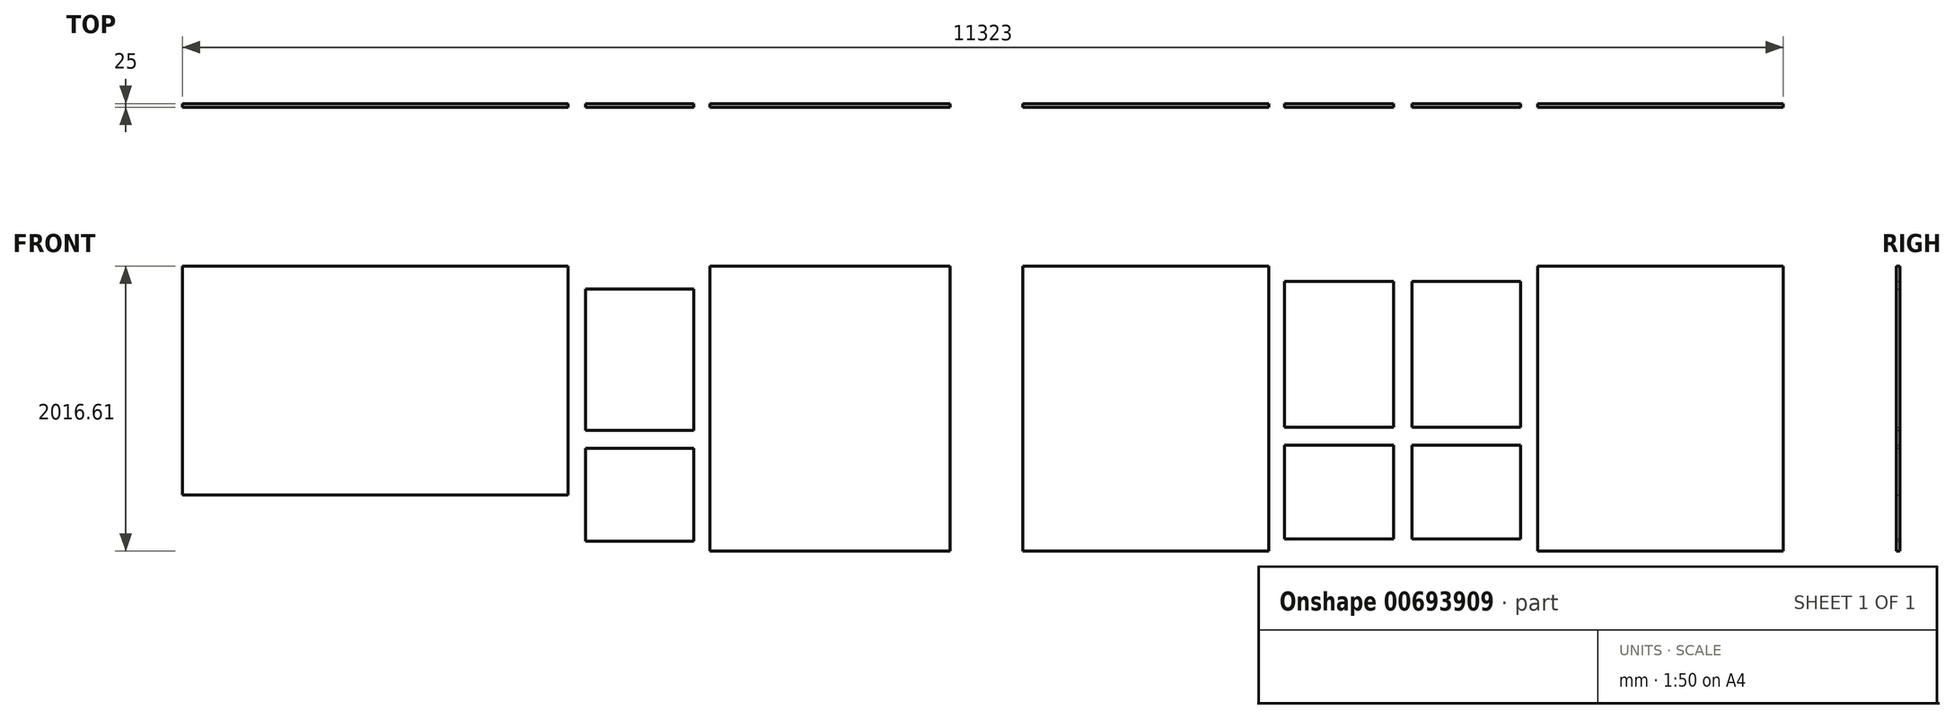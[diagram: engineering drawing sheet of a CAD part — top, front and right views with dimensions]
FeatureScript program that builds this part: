
annotation { "Feature Type Name" : "Feature", "Feature Type Description" : "" }
export const myFeature = defineFeature(function(context is Context, id is Id, definition is map)
    precondition{}
    {
        {
            var Q0;
            Q0=qCreatedBy(makeId("Front.planeOp"),FACE);
            var sketch = newSketch(context, id + "F0", { "sketchPlane" : qUnion([Q0])});
            skLineSegment(sketch, "E0.bottom", {"start": v(514, 2060.6) * mm, "end": v(2253, 2060.6) * mm});
            skLineSegment(sketch, "E0.top", {"start": v(514, 44) * mm, "end": v(2253, 44) * mm});
            skLineSegment(sketch, "E0.left", {"start": v(514, 2060.6) * mm, "end": v(514, 44) * mm});
            skLineSegment(sketch, "E0.right", {"start": v(2253, 2060.6) * mm, "end": v(2253, 44) * mm});
            skLineSegment(sketch, "E1.bottom", {"start": v(2365, 795) * mm, "end": v(3135, 795) * mm});
            skLineSegment(sketch, "E1.top", {"start": v(2365, 130) * mm, "end": v(3135, 130) * mm});
            skLineSegment(sketch, "E1.left", {"start": v(2365, 795) * mm, "end": v(2365, 130) * mm});
            skLineSegment(sketch, "E1.right", {"start": v(3135, 795) * mm, "end": v(3135, 130) * mm});
            skLineSegment(sketch, "E2.bottom", {"start": v(3266, 795) * mm, "end": v(4036, 795) * mm});
            skLineSegment(sketch, "E2.top", {"start": v(3266, 130) * mm, "end": v(4036, 130) * mm});
            skLineSegment(sketch, "E2.left", {"start": v(3266, 795) * mm, "end": v(3266, 130) * mm});
            skLineSegment(sketch, "E2.right", {"start": v(4036, 795) * mm, "end": v(4036, 130) * mm});
            skLineSegment(sketch, "E3.bottom", {"start": v(3266, 1952.8) * mm, "end": v(4036, 1952.8) * mm});
            skLineSegment(sketch, "E3.top", {"start": v(3266, 921) * mm, "end": v(4036, 921) * mm});
            skLineSegment(sketch, "E3.left", {"start": v(3266, 1952.8) * mm, "end": v(3266, 921) * mm});
            skLineSegment(sketch, "E3.right", {"start": v(4036, 1952.8) * mm, "end": v(4036, 921) * mm});
            skLineSegment(sketch, "E4.bottom", {"start": v(2365, 1952.8) * mm, "end": v(3135, 1952.8) * mm});
            skLineSegment(sketch, "E4.top", {"start": v(2365, 921) * mm, "end": v(3135, 921) * mm});
            skLineSegment(sketch, "E4.left", {"start": v(2365, 1952.8) * mm, "end": v(2365, 921) * mm});
            skLineSegment(sketch, "E4.right", {"start": v(3135, 1952.8) * mm, "end": v(3135, 921) * mm});
            skLineSegment(sketch, "E5.bottom", {"start": v(4156, 2060.6) * mm, "end": v(5892, 2060.6) * mm});
            skLineSegment(sketch, "E5.top", {"start": v(4156, 44) * mm, "end": v(5892, 44) * mm});
            skLineSegment(sketch, "E5.left", {"start": v(4156, 2060.6) * mm, "end": v(4156, 44) * mm});
            skLineSegment(sketch, "E5.right", {"start": v(5892, 2060.6) * mm, "end": v(5892, 44) * mm});
            skLineSegment(sketch, "E6.bottom", {"start": v(-1700, 2060.6) * mm, "end": v(0, 2060.6) * mm});
            skLineSegment(sketch, "E6.top", {"start": v(-1700, 44) * mm, "end": v(0, 44) * mm});
            skLineSegment(sketch, "E6.left", {"start": v(-1700, 2060.6) * mm, "end": v(-1700, 44) * mm});
            skLineSegment(sketch, "E6.right", {"start": v(0, 2060.6) * mm, "end": v(0, 44) * mm});
            skLineSegment(sketch, "E7.bottom", {"start": v(-2579, 1898) * mm, "end": v(-1814, 1898) * mm});
            skLineSegment(sketch, "E7.top", {"start": v(-2579, 898) * mm, "end": v(-1814, 898) * mm});
            skLineSegment(sketch, "E7.left", {"start": v(-2579, 1898) * mm, "end": v(-2579, 898) * mm});
            skLineSegment(sketch, "E7.right", {"start": v(-1814, 1898) * mm, "end": v(-1814, 898) * mm});
            skLineSegment(sketch, "E8.bottom", {"start": v(-2579, 772) * mm, "end": v(-1814, 772) * mm});
            skLineSegment(sketch, "E8.top", {"start": v(-2579, 114) * mm, "end": v(-1814, 114) * mm});
            skLineSegment(sketch, "E8.left", {"start": v(-2579, 772) * mm, "end": v(-2579, 114) * mm});
            skLineSegment(sketch, "E8.right", {"start": v(-1814, 772) * mm, "end": v(-1814, 114) * mm});
            skLineSegment(sketch, "E9.bottom", {"start": v(-2701, 2060.6) * mm, "end": v(-5431, 2060.6) * mm});
            skLineSegment(sketch, "E9.top", {"start": v(-2701, 442) * mm, "end": v(-5431, 442) * mm});
            skLineSegment(sketch, "E9.left", {"start": v(-2701, 2060.6) * mm, "end": v(-2701, 442) * mm});
            skLineSegment(sketch, "E9.right", {"start": v(-5431, 2060.6) * mm, "end": v(-5431, 442) * mm});
            skSolve(sketch);
        }
        {
            var Q0;
            Q0 = qSketchRegion(id + "F0", true);
            extrude(context, id + "F1", {"entities" : qUnion([Q0]), "depth" : 25 * mm, "offsetDistance" : 25 * mm});
        }
    });
